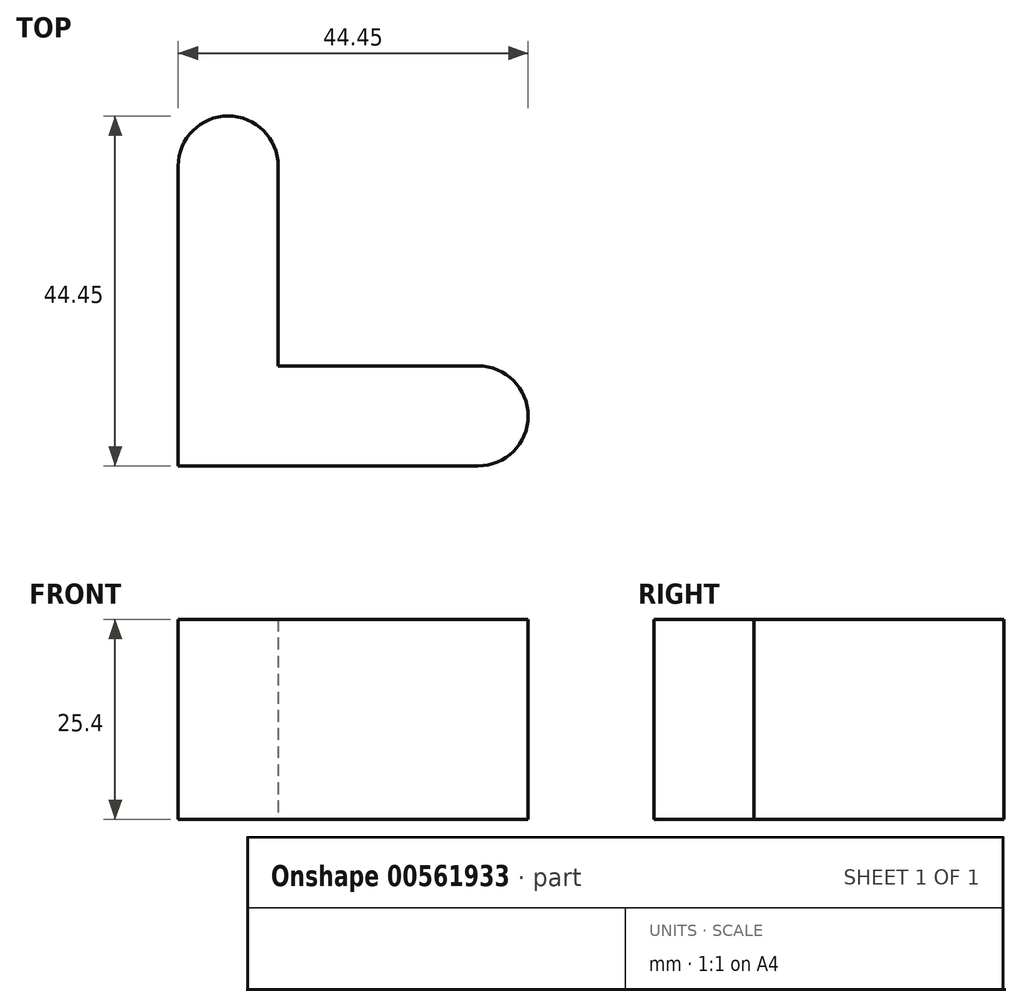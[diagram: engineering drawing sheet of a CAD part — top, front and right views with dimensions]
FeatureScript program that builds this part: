
annotation { "Feature Type Name" : "Feature", "Feature Type Description" : "" }
export const myFeature = defineFeature(function(context is Context, id is Id, definition is map)
    precondition{}
    {
        {
            var Q0;
            Q0=qCreatedBy(makeId("Top.planeOp"),FACE);
            var sketch = newSketch(context, id + "F0", { "sketchPlane" : qUnion([Q0])});
            skLineSegment(sketch, "E0.bottom", {"start": v(0, 0) * mm, "end": v(38.1, 0) * mm});
            skLineSegment(sketch, "E0.top", {"start": v(0, 12.7) * mm, "end": v(38.1, 12.7) * mm});
            skLineSegment(sketch, "E0.left", {"start": v(0, 0) * mm, "end": v(0, 12.7) * mm});
            skLineSegment(sketch, "E0.right", {"start": v(38.1, 0) * mm, "end": v(38.1, 12.7) * mm});
            skLineSegment(sketch, "E1.bottom", {"start": v(0, 0) * mm, "end": v(12.7, 0) * mm});
            skLineSegment(sketch, "E1.top", {"start": v(0, 38.1) * mm, "end": v(12.7, 38.1) * mm});
            skLineSegment(sketch, "E1.left", {"start": v(0, 0) * mm, "end": v(0, 38.1) * mm});
            skLineSegment(sketch, "E1.right", {"start": v(12.7, 0) * mm, "end": v(12.7, 38.1) * mm});
            skCircle(sketch, "E2", {"center": v(38.1, 6.35) * mm, "radius": 6.35 * mm});
            skCircle(sketch, "E3", {"center": v(6.35, 38.1) * mm, "radius": 6.35 * mm});
            skLineSegment(sketch, "E4", {"start": v(0, 12.7) * mm, "end": v(6.35, 12.7) * mm});
            skLineSegment(sketch, "E5", {"start": v(12.7, 6.35) * mm, "end": v(12.7, 0) * mm});
            skPoint(sketch, "E6.visualSharp", {"position": v(12.7, 12.7) * mm});
            skArc(sketch, "E6.filletArc", {"start": v(12.7, 6.35) * mm, "mid": v(10.84, 10.84) * mm, "end": v(6.35, 12.7) * mm});
            skLineSegment(sketch, "E7", {"start": v(12.7, 12.7) * mm, "end": v(23.62, 12.7) * mm});
            skLineSegment(sketch, "E8", {"start": v(18.16, 12.7) * mm, "end": v(12.7, 12.7) * mm});
            skLineSegment(sketch, "E9", {"start": v(12.7, 19.05) * mm, "end": v(12.7, 12.7) * mm});
            skPoint(sketch, "E10.endSnap0", {"position": v(15.43, 15.88) * mm});
            skSolve(sketch);
        }
        {
            var Q0;
            Q0 = qSketchRegion(id + "F0", true);
            extrude(context, id + "F1", {"entities" : qUnion([Q0]), "depth" : 25.4 * mm, "offsetDistance" : 25.4 * mm});
        }
    });
